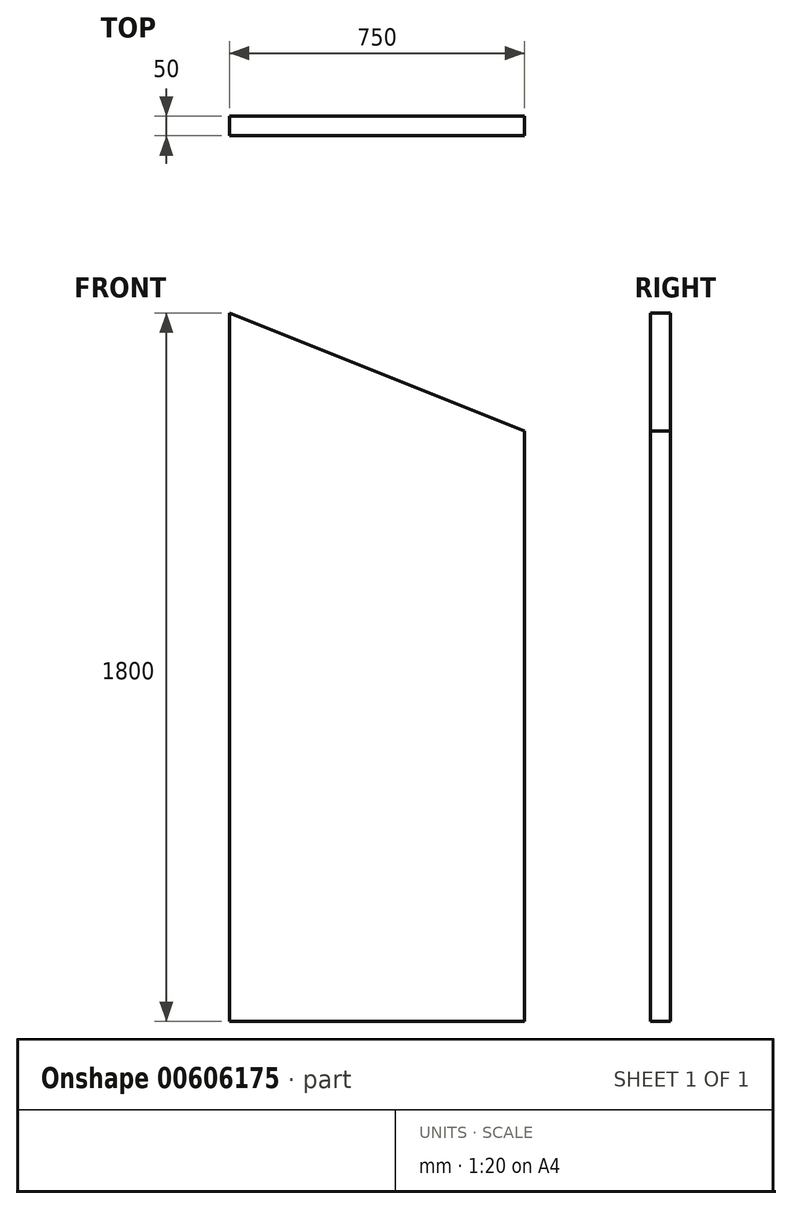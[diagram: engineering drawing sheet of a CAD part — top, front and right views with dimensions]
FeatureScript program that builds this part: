
annotation { "Feature Type Name" : "Feature", "Feature Type Description" : "" }
export const myFeature = defineFeature(function(context is Context, id is Id, definition is map)
    precondition{}
    {
        {
            var Q0;
            Q0=qCreatedBy(makeId("Front.planeOp"),FACE);
            var sketch = newSketch(context, id + "F0", { "sketchPlane" : qUnion([Q0])});
            skLineSegment(sketch, "E0.top", {"start": v(375, -900) * mm, "end": v(-375, -900) * mm});
            skLineSegment(sketch, "E0.right", {"start": v(-375, 900) * mm, "end": v(-375, -900) * mm});
            skPoint(sketch, "E0.middle", {"position": v(0, 0) * mm});
            skLineSegment(sketch, "E1", {"start": v(375, 600) * mm, "end": v(-375, 900) * mm});
            skLineSegment(sketch, "E2", {"start": v(375, 600) * mm, "end": v(375, -900) * mm});
            skSolve(sketch);
        }
        {
            var Q0;
            Q0=qSketchRegion(id+"F0",true);
            extrude(context, id + "F1", {"entities" : qUnion([Q0]), "depth" : 50 * mm, "offsetDistance" : 25.4 * mm});
        }
    });
